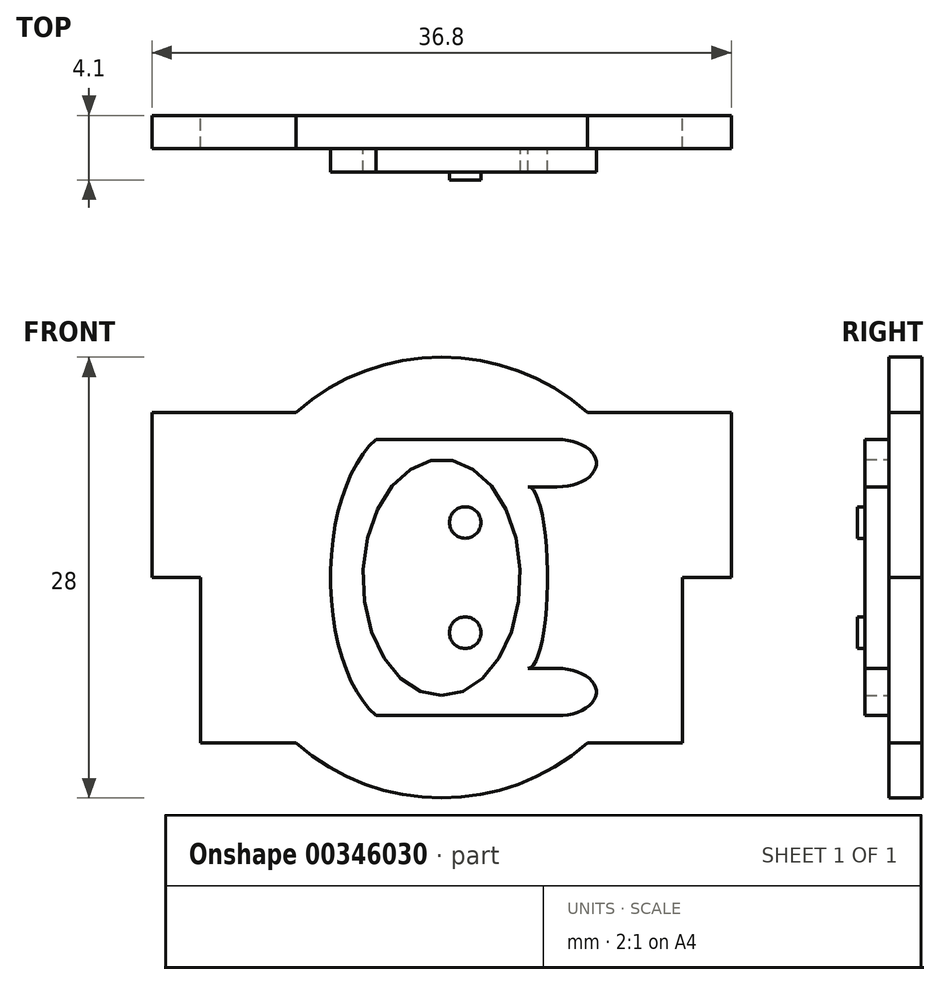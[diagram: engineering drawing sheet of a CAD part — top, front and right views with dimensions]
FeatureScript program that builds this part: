
annotation { "Feature Type Name" : "Feature", "Feature Type Description" : "" }
export const myFeature = defineFeature(function(context is Context, id is Id, definition is map)
    precondition{}
    {
        {
            var Q0;
            Q0=qCreatedBy(makeId("Front.planeOp"),FACE);
            var sketch = newSketch(context, id + "F0", { "sketchPlane" : qUnion([Q0])});
            skPoint(sketch, "E0.orphan", {"position": v(10.34, 0.81) * mm});
            skPoint(sketch, "E1.orphan", {"position": v(-10.34, 0.81) * mm});
            skPoint(sketch, "E2.start.orphan", {"position": v(0, 15.07) * mm});
            skPoint(sketch, "E3.start.orphan", {"position": v(0, -18.12) * mm});
            skPoint(sketch, "E4.start.orphan", {"position": v(12.18, 0) * mm});
            skArc(sketch, "E5", {"start": v(9.26, 10.5) * mm, "mid": v(0, 14) * mm, "end": v(-9.26, 10.5) * mm});
            skLineSegment(sketch, "E6", {"start": v(18.4, 10.5) * mm, "end": v(9.26, 10.5) * mm});
            skLineSegment(sketch, "E7", {"start": v(-18.4, 10.5) * mm, "end": v(-18.4, 0) * mm});
            skLineSegment(sketch, "E8", {"start": v(-18.4, 0) * mm, "end": v(-15.3, 0) * mm});
            skLineSegment(sketch, "E9", {"start": v(-15.3, 0) * mm, "end": v(-15.3, -10.5) * mm});
            skLineSegment(sketch, "E10", {"start": v(-15.3, -10.5) * mm, "end": v(-9.26, -10.5) * mm});
            skLineSegment(sketch, "E11", {"start": v(15.3, -10.5) * mm, "end": v(15.3, 0) * mm});
            skLineSegment(sketch, "E12", {"start": v(15.3, 0) * mm, "end": v(18.4, 0) * mm});
            skLineSegment(sketch, "E13", {"start": v(18.4, 0) * mm, "end": v(18.4, 10.5) * mm});
            skArc(sketch, "E14.trimOffspring", {"start": v(-9.26, -10.5) * mm, "mid": v(0, -14) * mm, "end": v(9.26, -10.5) * mm});
            skLineSegment(sketch, "E15.trimOffspring", {"start": v(-9.26, 10.5) * mm, "end": v(-18.4, 10.5) * mm});
            skLineSegment(sketch, "E16.trimOffspring", {"start": v(9.26, -10.5) * mm, "end": v(15.3, -10.5) * mm});
            skSolve(sketch);
        }
        {
            var Q0;
            Q0=makeQuery(id+"F0.imprint","IMPRINT",FACE,{"disambiguationData":[TD([[makeQuery(id+"F0.imprint","IMPRINT",EDGE,{"derivedFrom":sQuery(id+"F0.wireOp",EDGE,"E5")}),1.0]])]});
            extrude(context, id + "F1", {"entities" : qUnion([Q0]), "depth" : 2.1 * mm});
        }
        {
            var Q0;
            Q0=makeQuery(id+"F1.opExtrude","CAP_FACE",FACE,{"disambiguationData":[OSD([sQuery(id+"F0.wireOp",EDGE,"E5"),sQuery(id+"F0.wireOp",EDGE,"E6"),sQuery(id+"F0.wireOp",EDGE,"E7"),sQuery(id+"F0.wireOp",EDGE,"E8"),sQuery(id+"F0.wireOp",EDGE,"E9"),sQuery(id+"F0.wireOp",EDGE,"E10"),sQuery(id+"F0.wireOp",EDGE,"E11"),sQuery(id+"F0.wireOp",EDGE,"E12"),sQuery(id+"F0.wireOp",EDGE,"E13"),sQuery(id+"F0.wireOp",EDGE,"E14.trimOffspring"),sQuery(id+"F0.wireOp",EDGE,"E15.trimOffspring"),sQuery(id+"F0.wireOp",EDGE,"E16.trimOffspring")])],"isStart":false});
            var sketch = newSketch(context, id + "F2", { "sketchPlane" : qUnion([Q0])});
            skEllipse(sketch, "E17", {"center": v(0, 0) * mm, "majorRadius": 7.5 * mm, "minorRadius": 5 * mm, "majorAxis": v(0, -1)});
            skEllipticalArc(sketch, "E18", {});
            skPoint(sketch, "E18.centerSnap0", {"position": v(-5, 0) * mm});
            skPoint(sketch, "E19.end.orphan", {"position": v(-3.27, 7.1) * mm});
            skPoint(sketch, "E20.end.orphan", {"position": v(-3.27, -7.89) * mm});
            skLineSegment(sketch, "E21", {"start": v(-4.16, 8.77) * mm, "end": v(7.34, 8.77) * mm});
            skLineSegment(sketch, "E22", {"start": v(7.34, 5.77) * mm, "end": v(5.5, 5.77) * mm});
            skLineSegment(sketch, "E23", {"start": v(5.5, -5.77) * mm, "end": v(7.34, -5.77) * mm});
            skLineSegment(sketch, "E24", {"start": v(7.34, -8.77) * mm, "end": v(-4.16, -8.77) * mm});
            skEllipticalArc(sketch, "E25", {});
            skEllipticalArc(sketch, "E26", {});
            skPoint(sketch, "E26.majorAxisSnap0", {"position": v(7.34, -7.27) * mm});
            skPoint(sketch, "E26.majorAxisSnap1", {"position": v(4.84, 7.27) * mm});
            skEllipticalArc(sketch, "E27", {});
            skPoint(sketch, "E27.centerSnap0", {"position": v(5, 0) * mm});
            skEllipticalArc(sketch, "E28.trimOffspring", {});
            skEllipticalArc(sketch, "E29", {});
            const initialGuessF2  = {"E18": [-0.0023483619588906004, 0, 0, -1, 0.009506115047799883, 0.004706266657542192, 3.537658729962709, 5.88711923080667], "E25": [0.007335998227577656, 0.007270206803998517, -1, 0, 0.0025, 0.0015, 1.5707963267948966, 4.71238898038469], "E26": [0.007335998227577658, -0.007270206803998536, -1, 0, 0.0025, 0.0015, 1.5707963267948966, 4.71238898038469], "E27": [0.005499544764268672, 0, 7.889417924703274e-05, -0.9999999968878543, 0.005770206821956261, 0.0005233934745515583, 4.59509163187582, 4.829412139414479], "E28.trimOffspring": [0.005499544764268672, 0, 7.889417924703274e-05, -0.9999999968878543, 0.005770206821956261, 0.0005233934745515583, 3.1398530995446268, 3.1415926535897936], "E29": [0.005499544764268672, 0, 7.889417924703272e-05, -0.9999999968878542, 0.005770206821956262, 0.0012202649089873827, 0, 3.141592653589793]};
            skSetInitialGuess(sketch, initialGuessF2);
            skSolve(sketch);
        }
        {
            var Q0;
            Q0=makeQuery(id+"F2.imprint","IMPRINT",FACE,{"disambiguationData":[TD([[makeQuery(id+"F2.imprint","IMPRINT",EDGE,{"derivedFrom":sQuery(id+"F2.wireOp",EDGE,"E18")}),1.0]])]});
            extrude(context, id + "F3", {"entities" : qUnion([Q0]), "operationType" : NewBodyOperationType.ADD, "depth" : 1.5 * mm});
        }
        {
            var Q0;
            Q0=makeQuery(id+"F3.opExtrude","CAP_FACE",FACE,{"disambiguationData":[OSD([sQuery(id+"F2.wireOp",EDGE,"E17"),sQuery(id+"F2.wireOp",EDGE,"E18"),sQuery(id+"F2.wireOp",EDGE,"E21"),sQuery(id+"F2.wireOp",EDGE,"E22"),sQuery(id+"F2.wireOp",EDGE,"E23"),sQuery(id+"F2.wireOp",EDGE,"E24"),sQuery(id+"F2.wireOp",EDGE,"E25"),sQuery(id+"F2.wireOp",EDGE,"E26"),sQuery(id+"F2.wireOp",EDGE,"E29")])],"isStart":false});
            var sketch = newSketch(context, id + "F4", { "sketchPlane" : qUnion([Q0])});
            skCircle(sketch, "E30", {"center": v(1.5, 3.5) * mm, "radius": 1 * mm});
            skCircle(sketch, "E31", {"center": v(1.5, -3.5) * mm, "radius": 1 * mm});
            skSolve(sketch);
        }
        {
            var Q0;
            Q0=makeQuery(id+"F4.imprint","IMPRINT",FACE,{"disambiguationData":[TD([[makeQuery(id+"F4.imprint","IMPRINT",EDGE,{"derivedFrom":sQuery(id+"F4.wireOp",EDGE,"E30")}),1.0]])]});
            var Q1;
            Q1=makeQuery(id+"F4.imprint","IMPRINT",FACE,{"disambiguationData":[TD([[makeQuery(id+"F4.imprint","IMPRINT",EDGE,{"derivedFrom":sQuery(id+"F4.wireOp",EDGE,"E31")}),1.0]])]});
            extrude(context, id + "F5", {"entities" : qUnion([Q0, Q1]), "operationType" : NewBodyOperationType.ADD, "depth" : 0.5 * mm});
        }
        {
            var Q0;
            Q0=makeQuery(id+"F3.opExtrude","CAP_FACE",FACE,{"disambiguationData":[OSD([sQuery(id+"F2.wireOp",EDGE,"E17"),sQuery(id+"F2.wireOp",EDGE,"E18"),sQuery(id+"F2.wireOp",EDGE,"E21"),sQuery(id+"F2.wireOp",EDGE,"E22"),sQuery(id+"F2.wireOp",EDGE,"E23"),sQuery(id+"F2.wireOp",EDGE,"E24"),sQuery(id+"F2.wireOp",EDGE,"E25"),sQuery(id+"F2.wireOp",EDGE,"E26"),sQuery(id+"F2.wireOp",EDGE,"E29")])],"isStart":false});
            var sketch = newSketch(context, id + "F6", { "sketchPlane" : qUnion([Q0])});
            skEllipticalArc(sketch, "E32", {});
            skEllipticalArc(sketch, "E33", {});
            skEllipticalArc(sketch, "E34", {});
            skPoint(sketch, "E34.centerSnap0", {"position": v(-1.5, 0) * mm});
            skPoint(sketch, "E35.center.orphan", {"position": v(-2.41, -0.99) * mm});
            skArc(sketch, "E36", {"start": v(-1.14, 1.9) * mm, "mid": v(-0.92, 2.55) * mm, "end": v(-1.35, 3.09) * mm});
            skEllipticalArc(sketch, "E37", {});
            skEllipticalArc(sketch, "E38", {});
            skFitSpline(sketch, "E39", {"points": [v(-3.47, -1.61) * mm, v(-3.47, -1.63) * mm, v(-3.46, -1.64) * mm, v(-3.45, -1.67) * mm, v(-3.44, -1.7) * mm, v(-3.43, -1.72) * mm, v(-3.42, -1.74) * mm, v(-3.4, -1.77) * mm, v(-3.39, -1.8) * mm, v(-3.38, -1.84) * mm], "startDerivative": vector(0.03, -0.2) * mm, "endDerivative": vector(0.1, -0.25) * mm});
            skArc(sketch, "E40", {"start": v(-1.7, -3.32) * mm, "mid": v(-0.93, -2.81) * mm, "end": v(-1.1, -1.92) * mm});
            const initialGuessF6  = {"E32": [-0.0026619420386850834, 0, 0, -1, 0.002226208569481969, 0.0011675626613838006, 3.7235387287490997, 5.520817604902472], "E33": [-0.002414077753201127, 0.0014563456643372774, -0.5795237969051341, -0.8149553170699955, 0.001955214982468451, 0.0009631922824800902, 3.2202187054584916, 4.808067543595664], "E34": [-0.000785255862865597, 0, 0, -1, 0.001978344516828656, 0.001299567390825814, 3.41485809048667, 6.0361086445733685], "E37": [-0.0023255725391209126, -0.0024287656415253878, 0.774257133063476, -0.6328711495243933, 0.0013148265113464906, 0.00048018508188800446, 3.5865706699386033, 5.637120153709596], "E38": [-0.003417565720155835, -0.0016591406892985106, 0.36039859555222176, -0.9327983985427859, 0.00010439045226524122, 3.753277382265707e-05, 4.050933246401616, 5.120169171820856]};
            skSetInitialGuess(sketch, initialGuessF6);
            skSolve(sketch);
        }
        {
            var Q0;
            {var subQ0=sQuery(id+"F6.wireOp",EDGE,"E32");Q0=makeQuery(id+"F6.imprint","IMPRINT",FACE,{"disambiguationData":[TD([[makeQuery(id+"F6.imprint","IMPRINT",EDGE,{"derivedFrom":subQ0}),1.0]])]});}
            extrude(context, id + "F7", {"entities" : qUnion([Q0]), "operationType" : NewBodyOperationType.REMOVE, "oppositeDirection" : true, "depth" : 0.5 * mm});
        }
    });
